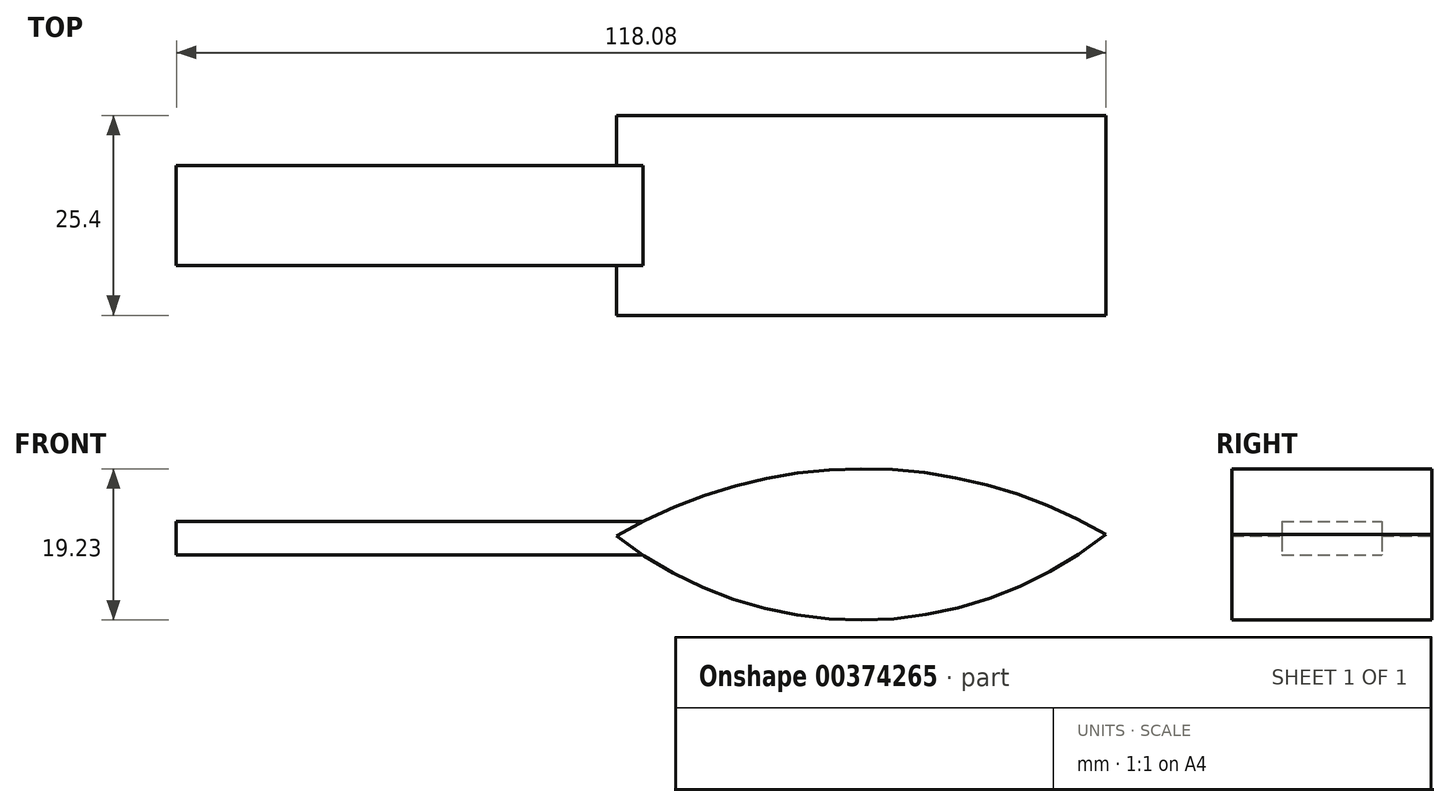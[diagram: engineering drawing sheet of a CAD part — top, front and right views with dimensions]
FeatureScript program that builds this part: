
annotation { "Feature Type Name" : "Feature", "Feature Type Description" : "" }
export const myFeature = defineFeature(function(context is Context, id is Id, definition is map)
    precondition{}
    {
        {
            var Q0;
            Q0=qCreatedBy(makeId("Front.planeOp"),FACE);
            var sketch = newSketch(context, id + "F0", { "sketchPlane" : qUnion([Q0])});
            skArc(sketch, "E0", {"start": v(52.05, 22.9) * mm, "mid": v(20.93, 31.2) * mm, "end": v(-10.12, 22.65) * mm});
            skArc(sketch, "E1", {"start": v(-10.12, 22.65) * mm, "mid": v(21, 11.98) * mm, "end": v(52.05, 22.9) * mm});
            skLineSegment(sketch, "E2", {"start": v(-6.77, 20.24) * mm, "end": v(-66.03, 20.24) * mm});
            skLineSegment(sketch, "E3", {"start": v(-6.77, 24.5) * mm, "end": v(-66.03, 24.5) * mm});
            skLineSegment(sketch, "E4", {"start": v(-66.03, 24.5) * mm, "end": v(-66.03, 20.24) * mm});
            skSolve(sketch);
        }
        {
            var Q0;
            Q0=makeQuery(id+"F0.imprint","IMPRINT",FACE,{"disambiguationData":[TD([[makeQuery(id+"F0.imprint","IMPRINT",EDGE,{"derivedFrom":sQuery(id+"F0.wireOp",EDGE,"E0")}),1.0]])]});
            extrude(context, id + "F1", {"entities" : qUnion([Q0]), "endBound" : BoundingType.SYMMETRIC, "depth" : 25.4 * mm});
        }
        {
            var Q0;
            {var subQ1=sQuery(id+"F0.wireOp",EDGE,"E2");Q0=makeQuery(id+"F0.imprint","IMPRINT",FACE,{"disambiguationData":[TD([[makeQuery(id+"F0.imprint","IMPRINT",EDGE,{"derivedFrom":subQ1}),-1.0]])]});}
            extrude(context, id + "F2", {"entities" : qUnion([Q0]), "operationType" : NewBodyOperationType.ADD, "endBound" : BoundingType.SYMMETRIC, "depth" : 12.7 * mm});
        }
    });
